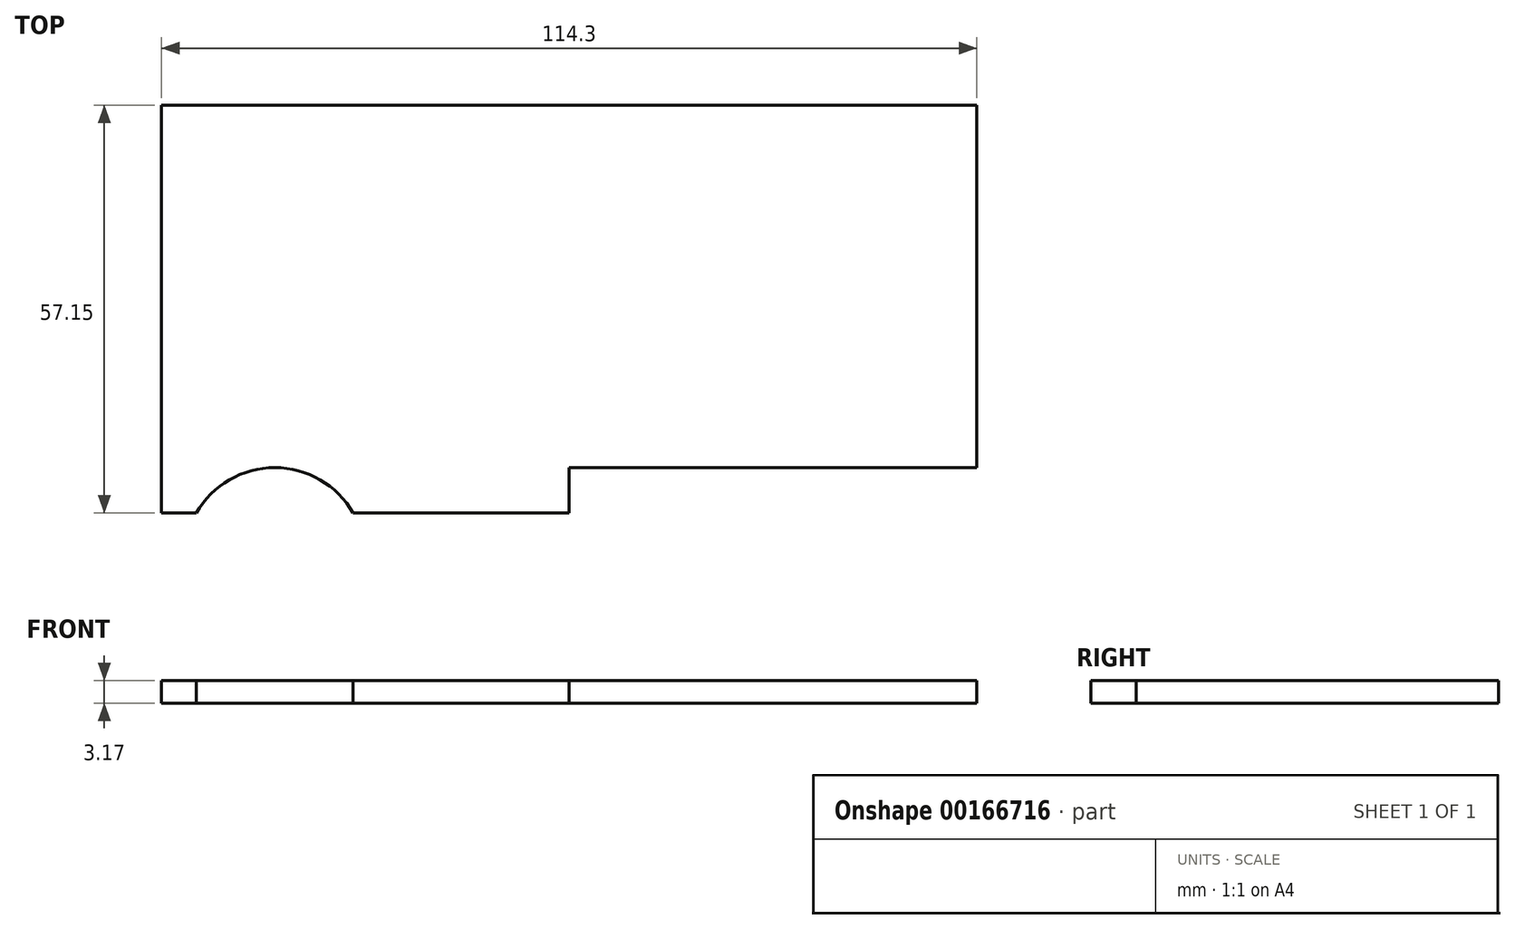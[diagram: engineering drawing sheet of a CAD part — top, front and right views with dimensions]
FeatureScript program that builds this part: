
annotation { "Feature Type Name" : "Feature", "Feature Type Description" : "" }
export const myFeature = defineFeature(function(context is Context, id is Id, definition is map)
    precondition{}
    {
        {
            var Q0;
            Q0=qCreatedBy(makeId("Top.planeOp"),FACE);
            var sketch = newSketch(context, id + "F0", { "sketchPlane" : qUnion([Q0])});
            skLineSegment(sketch, "E0", {"start": v(0, 0) * mm, "end": v(0, 25.4) * mm, "construction": true});
            skLineSegment(sketch, "E1", {"start": v(-57.15, 25.4) * mm, "end": v(57.15, 25.4) * mm});
            skLineSegment(sketch, "E2", {"start": v(-57.15, 25.4) * mm, "end": v(-57.15, -31.75) * mm});
            skLineSegment(sketch, "E3", {"start": v(-57.15, -31.75) * mm, "end": v(-52.27, -31.75) * mm});
            skLineSegment(sketch, "E4", {"start": v(-30.28, -31.75) * mm, "end": v(0, -31.75) * mm});
            skLineSegment(sketch, "E5", {"start": v(0, -31.75) * mm, "end": v(0, -25.4) * mm});
            skLineSegment(sketch, "E6", {"start": v(0, -25.4) * mm, "end": v(57.15, -25.4) * mm});
            skLineSegment(sketch, "E7", {"start": v(57.15, -25.4) * mm, "end": v(57.15, 25.4) * mm});
            skLineSegment(sketch, "E8", {"start": v(0, 0) * mm, "end": v(57.15, 0) * mm, "construction": true});
            skArc(sketch, "E9", {"start": v(-30.28, -31.75) * mm, "mid": v(-41.28, -25.4) * mm, "end": v(-52.27, -31.75) * mm});
            skSolve(sketch);
        }
        {
            var Q0;
            Q0 = qSketchRegion(id + "F0", true);
            extrude(context, id + "F1", {"entities" : qUnion([Q0]), "depth" : 3.17 * mm});
        }
    });
